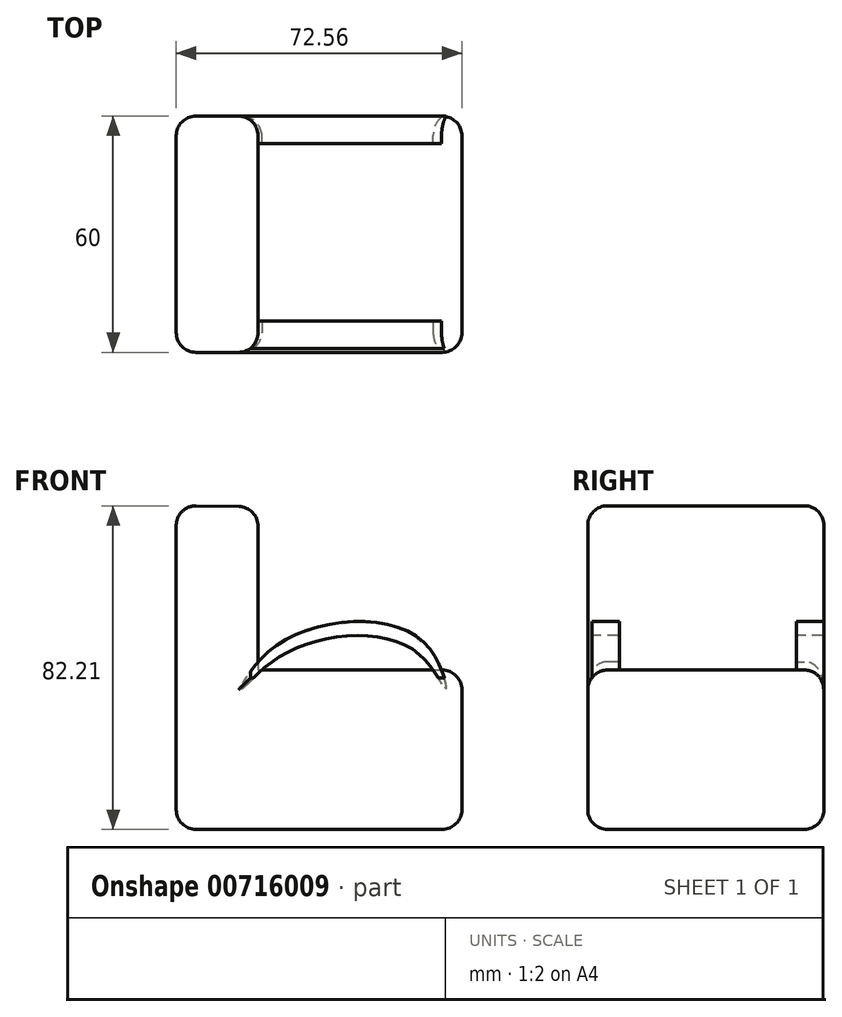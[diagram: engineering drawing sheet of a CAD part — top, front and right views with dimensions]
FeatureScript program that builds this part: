
annotation { "Feature Type Name" : "Feature", "Feature Type Description" : "" }
export const myFeature = defineFeature(function(context is Context, id is Id, definition is map)
    precondition{}
    {
        {
            var Q0;
            Q0=qCreatedBy(makeId("Front.planeOp"),FACE);
            var sketch = newSketch(context, id + "F0", { "sketchPlane" : qUnion([Q0])});
            skLineSegment(sketch, "E0", {"start": v(-37.14, 46.69) * mm, "end": v(-37.14, -35.61) * mm});
            skLineSegment(sketch, "E1", {"start": v(-37.14, -35.61) * mm, "end": v(35.42, -35.61) * mm});
            skLineSegment(sketch, "E2", {"start": v(35.42, -35.61) * mm, "end": v(35.42, 4.87) * mm});
            skLineSegment(sketch, "E3", {"start": v(35.42, 4.87) * mm, "end": v(-16.33, 4.87) * mm});
            skLineSegment(sketch, "E4", {"start": v(-16.33, 4.87) * mm, "end": v(-16.33, 46.3) * mm});
            skLineSegment(sketch, "E5", {"start": v(-16.33, 46.3) * mm, "end": v(-37.14, 46.69) * mm});
            skSolve(sketch);
        }
        {
            var Q0;
            Q0 = qSketchRegion(id + "F0", true);
            extrude(context, id + "F1", {"entities" : qUnion([Q0]), "depth" : 60 * mm, "offsetDistance" : 25 * mm});
        }
        {
            var Q0;
            Q0=makeQuery(id+"F1.opExtrude","CAP_EDGE",EDGE,{"disambiguationData":[OSD([sQuery(id+"F0.wireOp",EDGE,"E5")])],"isStart":false});
            var Q1;
            Q1=makeQuery(id+"F1.opExtrude","CAP_EDGE",EDGE,{"disambiguationData":[OSD([sQuery(id+"F0.wireOp",EDGE,"E4")])],"isStart":false});
            var Q2;
            Q2=makeQuery(id+"F1.opExtrude","CAP_EDGE",EDGE,{"disambiguationData":[OSD([sQuery(id+"F0.wireOp",EDGE,"E0")])],"isStart":false});
            var Q3;
            Q3=makeQuery(id+"F1.opExtrude","CAP_EDGE",EDGE,{"disambiguationData":[OSD([sQuery(id+"F0.wireOp",EDGE,"E1")])],"isStart":false});
            var Q4;
            Q4=makeQuery(id+"F1.opExtrude","CAP_FACE",FACE,{"disambiguationData":[OSD([sQuery(id+"F0.wireOp",EDGE,"E0"),sQuery(id+"F0.wireOp",EDGE,"E1"),sQuery(id+"F0.wireOp",EDGE,"E2"),sQuery(id+"F0.wireOp",EDGE,"E3"),sQuery(id+"F0.wireOp",EDGE,"E4"),sQuery(id+"F0.wireOp",EDGE,"E5")])],"isStart":false});
            var Q5;
            Q5=makeQuery(id+"F1.opExtrude","SWEPT_EDGE",EDGE,{"disambiguationData":[OSD([sQuery(id+"F0.wireOp",EDGE,"E0"),sQuery(id+"F0.wireOp",EDGE,"E5")])]});
            var Q6;
            Q6=makeQuery(id+"F1.opExtrude","CAP_EDGE",EDGE,{"disambiguationData":[OSD([sQuery(id+"F0.wireOp",EDGE,"E0")])],"isStart":true});
            var Q7;
            Q7=makeQuery(id+"F1.opExtrude","CAP_EDGE",EDGE,{"disambiguationData":[OSD([sQuery(id+"F0.wireOp",EDGE,"E4")])],"isStart":true});
            var Q8;
            Q8=makeQuery(id+"F1.opExtrude","CAP_EDGE",EDGE,{"disambiguationData":[OSD([sQuery(id+"F0.wireOp",EDGE,"E3")])],"isStart":true});
            var Q9;
            Q9=makeQuery(id+"F1.opExtrude","CAP_EDGE",EDGE,{"disambiguationData":[OSD([sQuery(id+"F0.wireOp",EDGE,"E2")])],"isStart":true});
            var Q10;
            Q10=makeQuery(id+"F1.opExtrude","CAP_EDGE",EDGE,{"disambiguationData":[OSD([sQuery(id+"F0.wireOp",EDGE,"E1")])],"isStart":true});
            var Q11;
            Q11=makeQuery(id+"F1.opExtrude","SWEPT_FACE",FACE,{"disambiguationData":[OSD([sQuery(id+"F0.wireOp",EDGE,"E2")])]});
            var Q12;
            Q12=makeQuery(id+"F1.opExtrude","SWEPT_EDGE",EDGE,{"disambiguationData":[OSD([sQuery(id+"F0.wireOp",EDGE,"E4"),sQuery(id+"F0.wireOp",EDGE,"E5")])]});
            var Q13;
            Q13=makeQuery(id+"F1.opExtrude","SWEPT_EDGE",EDGE,{"disambiguationData":[OSD([sQuery(id+"F0.wireOp",EDGE,"E0"),sQuery(id+"F0.wireOp",EDGE,"E1")])]});
            var Q14;
            Q14=makeQuery(id+"F1.opExtrude","CAP_EDGE",EDGE,{"disambiguationData":[OSD([sQuery(id+"F0.wireOp",EDGE,"E3")])],"isStart":false});
            var Q15;
            Q15=makeQuery(id+"F1.opExtrude","CAP_EDGE",EDGE,{"disambiguationData":[OSD([sQuery(id+"F0.wireOp",EDGE,"E5")])],"isStart":true});
            fillet(context, id + "F2", {"entities" : qUnion([Q0, Q1, Q2, Q3, Q4, Q5, Q6, Q7, Q8, Q9, Q10, Q11, Q12, Q13, Q14, Q15]), "radius" : 5 * mm, "tangentPropagation" : true, "allowEdgeOverflow" : false});
        }
        {
            var Q0;
            Q0=qCreatedBy(makeId("Front.planeOp"),FACE);
            var sketch = newSketch(context, id + "F3", { "sketchPlane" : qUnion([Q0])});
            skFitSpline(sketch, "E6", {"points": [v(-20.58, 0) * mm, v(-11.56, 11.18) * mm, v(25.1, 12.5) * mm, v(31.3, 0) * mm, v(23.59, 9.68) * mm, v(-10.06, 8.74) * mm, v(-20.58, 0) * mm]});
            skSolve(sketch);
        }
        {
            var Q0;
            Q0 = qSketchRegion(id + "F3", true);
            extrude(context, id + "F4", {"entities" : qUnion([Q0]), "depth" : 7 * mm, "offsetDistance" : 25 * mm});
        }
        {
            var Q0;
            Q0=qCreatedBy(makeId("Front.planeOp"),FACE);
            cPlane(context, id + "F5", {"entities" : qUnion([Q0]), "cplaneType" : CPlaneType.OFFSET, "offset" : 29.5 * mm, "width" : 150 * mm, "height" : 150 * mm});
        }
        {
            var Q0;
            Q0=makeQuery(id+"F4.opExtrude","SWEPT_BODY",BODY,{"disambiguationData":[OSD([sQuery(id+"F3.wireOp",EDGE,"E6")])]});
            var Q1;
            Q1=qCreatedBy(id+"F5.planeOp",FACE);
            mirror(context, id + "F6", {"operationType" : NewBodyOperationType.ADD, "entities" : qUnion([Q0]), "mirrorPlane" : qUnion([Q1])});
        }
    });
